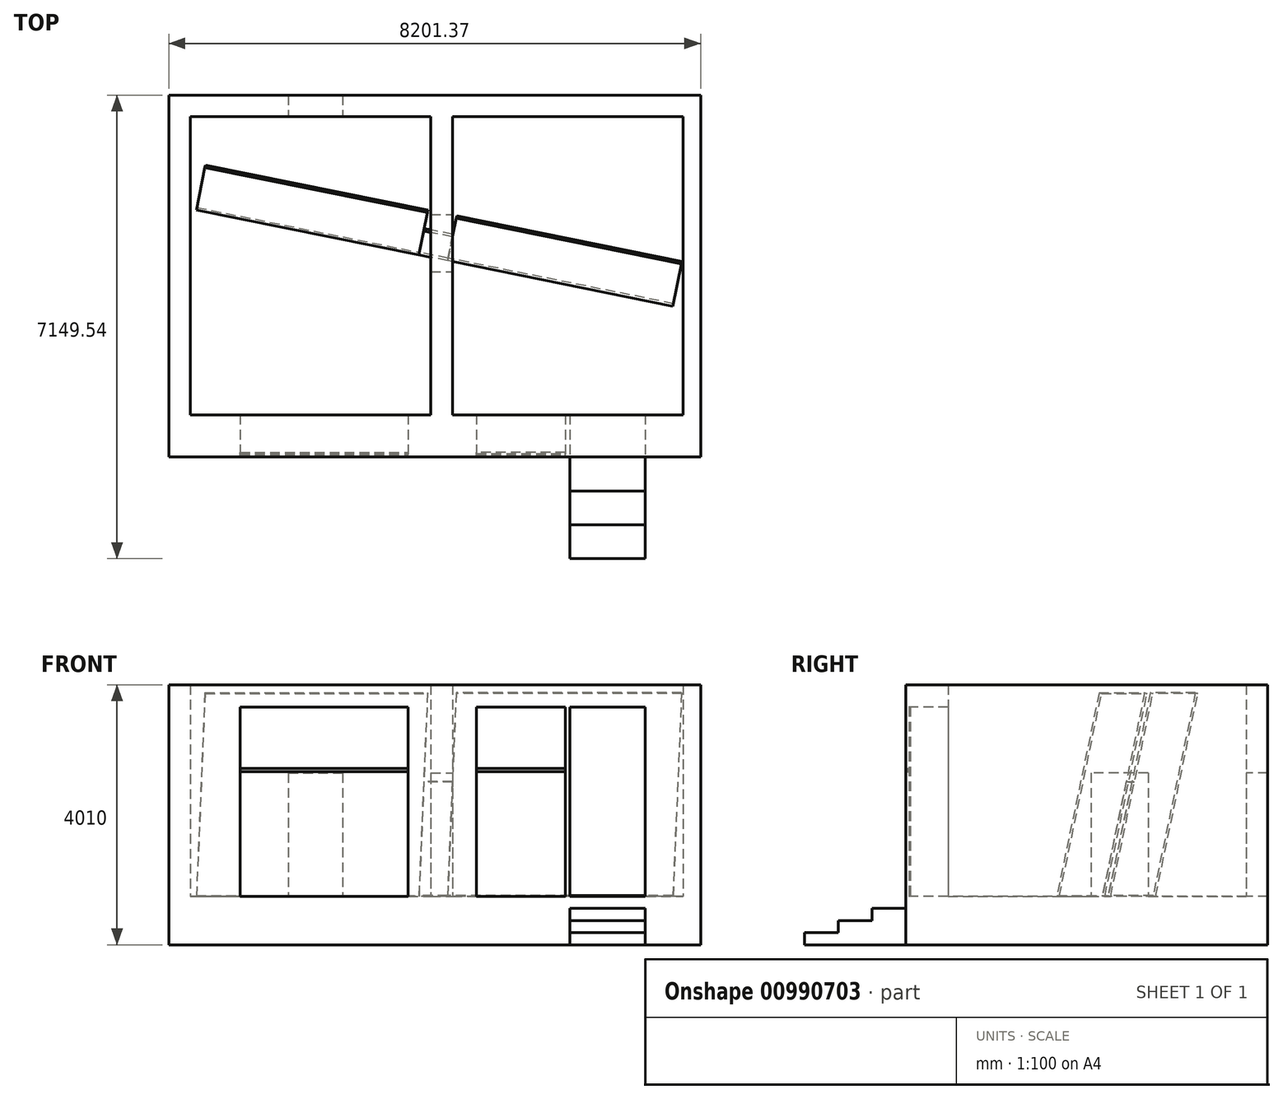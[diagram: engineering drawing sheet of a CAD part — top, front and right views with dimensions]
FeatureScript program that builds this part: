
annotation { "Feature Type Name" : "Feature", "Feature Type Description" : "" }
export const myFeature = defineFeature(function(context is Context, id is Id, definition is map)
    precondition{}
    {
        {
            var Q0;
            Q0=qCreatedBy(makeId("Top.planeOp"),FACE);
            var sketch = newSketch(context, id + "F0", { "sketchPlane" : qUnion([Q0])});
            skLineSegment(sketch, "E0", {"start": v(0, 440) * mm, "end": v(0, -440) * mm, "construction": true});
            skLineSegment(sketch, "E1", {"start": v(-165.82, 440) * mm, "end": v(165.82, 440) * mm});
            skLineSegment(sketch, "E2", {"start": v(-165.82, -440) * mm, "end": v(165.82, -440) * mm});
            skLineSegment(sketch, "E3", {"start": v(165.82, 440) * mm, "end": v(165.82, 1951.88) * mm});
            skLineSegment(sketch, "E4", {"start": v(165.82, 1951.88) * mm, "end": v(3725.82, 1951.88) * mm});
            skLineSegment(sketch, "E5", {"start": v(3725.82, 1951.88) * mm, "end": v(3725.82, -2648.12) * mm});
            skLineSegment(sketch, "E6", {"start": v(3725.82, -2648.12) * mm, "end": v(3139.18, -2648.12) * mm});
            skLineSegment(sketch, "E7", {"start": v(165.82, -2648.12) * mm, "end": v(165.82, -440) * mm});
            skLineSegment(sketch, "E8", {"start": v(-165.82, 440) * mm, "end": v(-165.82, 1951.88) * mm});
            skLineSegment(sketch, "E9", {"start": v(-165.82, 1951.88) * mm, "end": v(-1524.68, 1951.88) * mm});
            skLineSegment(sketch, "E10", {"start": v(-3875.82, 1951.88) * mm, "end": v(-3875.82, -2648.12) * mm});
            skLineSegment(sketch, "E11", {"start": v(-3875.82, -2648.12) * mm, "end": v(-3107.34, -2648.12) * mm});
            skLineSegment(sketch, "E12", {"start": v(-165.82, -2648.12) * mm, "end": v(-165.82, -440) * mm});
            skLineSegment(sketch, "E13", {"start": v(-4207.47, 2283.53) * mm, "end": v(-2364.74, 2283.53) * mm});
            skLineSegment(sketch, "E14", {"start": v(3993.9, 2283.53) * mm, "end": v(3993.9, -3299.43) * mm});
            skLineSegment(sketch, "E15", {"start": v(3993.9, -3299.43) * mm, "end": v(3139.18, -3299.43) * mm});
            skLineSegment(sketch, "E16", {"start": v(-4207.47, -3299.43) * mm, "end": v(-4207.47, 2283.53) * mm});
            skLineSegment(sketch, "E17", {"start": v(-3875.82, 1951.88) * mm, "end": v(-4207.47, 1951.88) * mm, "construction": true});
            skLineSegment(sketch, "E18", {"start": v(-3875.82, 1951.88) * mm, "end": v(-3875.82, 2283.53) * mm, "construction": true});
            skLineSegment(sketch, "E19", {"start": v(3725.82, -2648.12) * mm, "end": v(3725.82, -3299.43) * mm, "construction": true});
            skLineSegment(sketch, "E20", {"start": v(3725.82, -2648.12) * mm, "end": v(3993.9, -2648.12) * mm, "construction": true});
            skLineSegment(sketch, "E21", {"start": v(-2364.74, 2283.53) * mm, "end": v(-2364.74, 1951.88) * mm});
            skLineSegment(sketch, "E22", {"start": v(-1524.68, 2283.53) * mm, "end": v(-1524.68, 1951.88) * mm});
            skLineSegment(sketch, "E23.trimOffspring", {"start": v(-1524.68, 2283.53) * mm, "end": v(3993.9, 2283.53) * mm});
            skLineSegment(sketch, "E24.trimOffspring", {"start": v(-2364.74, 1951.88) * mm, "end": v(-3875.82, 1951.88) * mm});
            skLineSegment(sketch, "E25", {"start": v(-3107.34, -2648.12) * mm, "end": v(-3107.34, -3299.43) * mm});
            skLineSegment(sketch, "E26", {"start": v(-515.8, -2648.12) * mm, "end": v(-515.8, -3299.43) * mm});
            skLineSegment(sketch, "E27.trimOffspring", {"start": v(-515.8, -2648.12) * mm, "end": v(-165.82, -2648.12) * mm});
            skLineSegment(sketch, "E28.trimOffspring", {"start": v(-3107.34, -3299.43) * mm, "end": v(-4207.47, -3299.43) * mm});
            skLineSegment(sketch, "E29", {"start": v(537.35, -2648.12) * mm, "end": v(537.35, -3299.43) * mm});
            skLineSegment(sketch, "E30", {"start": v(1907.35, -2648.12) * mm, "end": v(1907.35, -3299.43) * mm});
            skLineSegment(sketch, "E31", {"start": v(1980.65, -2648.12) * mm, "end": v(1980.65, -3299.43) * mm});
            skLineSegment(sketch, "E32", {"start": v(3139.18, -2648.12) * mm, "end": v(3139.18, -3299.43) * mm});
            skLineSegment(sketch, "E33.trimOffspring", {"start": v(537.35, -2648.12) * mm, "end": v(165.82, -2648.12) * mm});
            skLineSegment(sketch, "E34.trimOffspring", {"start": v(537.35, -3299.43) * mm, "end": v(-515.8, -3299.43) * mm});
            skLineSegment(sketch, "E35.trimOffspring", {"start": v(1980.65, -2648.12) * mm, "end": v(1907.35, -2648.12) * mm});
            skLineSegment(sketch, "E36.trimOffspring", {"start": v(1980.65, -3299.43) * mm, "end": v(1907.35, -3299.43) * mm});
            skSolve(sketch);
        }
        {
            var Q0;
            Q0 = qSketchRegion(id + "F0", true);
            extrude(context, id + "F1", {"entities" : qUnion([Q0]), "depth" : 3260 * mm, "offsetDistance" : 25 * mm});
        }
        {
            var Q0;
            Q0=makeQuery(id+"F1.opExtrude","CAP_FACE",FACE,{"disambiguationData":[OSD([sQuery(id+"F0.wireOp",EDGE,"E10"),sQuery(id+"F0.wireOp",EDGE,"E11"),sQuery(id+"F0.wireOp",EDGE,"E13"),sQuery(id+"F0.wireOp",EDGE,"E16"),sQuery(id+"F0.wireOp",EDGE,"E21"),sQuery(id+"F0.wireOp",EDGE,"E24.trimOffspring"),sQuery(id+"F0.wireOp",EDGE,"E25"),sQuery(id+"F0.wireOp",EDGE,"E28.trimOffspring")])],"isStart":true});
            var sketch = newSketch(context, id + "F2", { "sketchPlane" : qUnion([Q0])});
            skLineSegment(sketch, "E37.bottom", {"start": v(-4207.47, 3299.43) * mm, "end": v(3993.9, 3299.43) * mm});
            skLineSegment(sketch, "E37.top", {"start": v(-4207.47, -2283.53) * mm, "end": v(3993.9, -2283.53) * mm});
            skLineSegment(sketch, "E37.left", {"start": v(-4207.47, 3299.43) * mm, "end": v(-4207.47, -2283.53) * mm});
            skLineSegment(sketch, "E37.right", {"start": v(3993.9, 3299.43) * mm, "end": v(3993.9, -2283.53) * mm});
            skSolve(sketch);
        }
        {
            var Q0;
            Q0 = qSketchRegion(id + "F2", true);
            extrude(context, id + "F3", {"entities" : qUnion([Q0]), "operationType" : NewBodyOperationType.ADD, "depth" : 750 * mm, "offsetDistance" : 25 * mm});
        }
        {
            var Q0;
            Q0=makeQuery(id+"F1.opExtrude","SWEPT_FACE",FACE,{"disambiguationData":[OSD([sQuery(id+"F0.wireOp",EDGE,"E32")])]});
            var sketch = newSketch(context, id + "F4", { "sketchPlane" : qUnion([Q0])});
            skLineSegment(sketch, "E38", {"start": v(3299.43, -187.5) * mm, "end": v(3821.63, -187.5) * mm});
            skLineSegment(sketch, "E39", {"start": v(3821.63, -187.5) * mm, "end": v(3821.63, -375) * mm});
            skLineSegment(sketch, "E40", {"start": v(3821.63, -375) * mm, "end": v(4343.82, -375) * mm});
            skLineSegment(sketch, "E41", {"start": v(4343.82, -375) * mm, "end": v(4343.82, -562.5) * mm});
            skLineSegment(sketch, "E42", {"start": v(4343.82, -562.5) * mm, "end": v(4866.01, -562.5) * mm});
            skLineSegment(sketch, "E43", {"start": v(4866.01, -562.5) * mm, "end": v(4866.01, -750) * mm});
            skLineSegment(sketch, "E44", {"start": v(4866.01, -750) * mm, "end": v(3299.43, -750) * mm});
            skLineSegment(sketch, "E45", {"start": v(3299.43, 0) * mm, "end": v(3299.43, -187.5) * mm, "construction": true});
            skLineSegment(sketch, "E46", {"start": v(3299.43, -187.5) * mm, "end": v(3299.43, -750) * mm});
            skSolve(sketch);
        }
        {
            var Q0;
            Q0 = qSketchRegion(id + "F4", true);
            var Q1;
            Q1=makeQuery(id+"F1.opExtrude","SWEPT_FACE",FACE,{"disambiguationData":[OSD([sQuery(id+"F0.wireOp",EDGE,"E31")])]});
            extrude(context, id + "F5", {"entities" : qUnion([Q0]), "operationType" : NewBodyOperationType.ADD, "endBound" : BoundingType.UP_TO_SURFACE, "depth" : 25 * mm, "endBoundEntityFace" : qUnion([Q1]), "offsetDistance" : 25 * mm});
        }
        {
            var Q0;
            Q0=makeQuery(id+"F1.opExtrude","CAP_FACE",FACE,{"disambiguationData":[OSD([sQuery(id+"F0.wireOp",EDGE,"E1"),sQuery(id+"F0.wireOp",EDGE,"E3"),sQuery(id+"F0.wireOp",EDGE,"E4"),sQuery(id+"F0.wireOp",EDGE,"E5"),sQuery(id+"F0.wireOp",EDGE,"E6"),sQuery(id+"F0.wireOp",EDGE,"E8"),sQuery(id+"F0.wireOp",EDGE,"E9"),sQuery(id+"F0.wireOp",EDGE,"E14"),sQuery(id+"F0.wireOp",EDGE,"E15"),sQuery(id+"F0.wireOp",EDGE,"E22"),sQuery(id+"F0.wireOp",EDGE,"E23.trimOffspring"),sQuery(id+"F0.wireOp",EDGE,"E32")])],"isStart":false});
            var sketch = newSketch(context, id + "F6", { "sketchPlane" : qUnion([Q0])});
            skLineSegment(sketch, "E47.bottom", {"start": v(-165.82, 440) * mm, "end": v(165.82, 440) * mm});
            skLineSegment(sketch, "E47.top", {"start": v(-165.82, -440) * mm, "end": v(165.82, -440) * mm});
            skLineSegment(sketch, "E47.left", {"start": v(-165.82, 440) * mm, "end": v(-165.82, -440) * mm});
            skLineSegment(sketch, "E47.right", {"start": v(165.82, 440) * mm, "end": v(165.82, -440) * mm});
            skSolve(sketch);
        }
        {
            var Q0;
            Q0 = qSketchRegion(id + "F6", true);
            var Q1;
            Q1=makeQuery(id+"F3.opExtrude","CAP_FACE",FACE,{"disambiguationData":[OSD([sQuery(id+"F2.wireOp",EDGE,"E37.bottom"),sQuery(id+"F2.wireOp",EDGE,"E37.top"),sQuery(id+"F2.wireOp",EDGE,"E37.left"),sQuery(id+"F2.wireOp",EDGE,"E37.right")])],"isStart":true});
            extrude(context, id + "F7", {"entities" : qUnion([Q0]), "operationType" : NewBodyOperationType.ADD, "endBound" : BoundingType.UP_TO_SURFACE, "oppositeDirection" : true, "depth" : 1120 * mm, "endBoundEntityFace" : qUnion([Q1]), "hasOffset" : true, "offsetDistance" : 1900 * mm});
        }
        {
            var Q0;
            Q0=makeQuery(id+"F1.opExtrude","CAP_FACE",FACE,{"disambiguationData":[OSD([sQuery(id+"F0.wireOp",EDGE,"E10"),sQuery(id+"F0.wireOp",EDGE,"E11"),sQuery(id+"F0.wireOp",EDGE,"E13"),sQuery(id+"F0.wireOp",EDGE,"E16"),sQuery(id+"F0.wireOp",EDGE,"E21"),sQuery(id+"F0.wireOp",EDGE,"E24.trimOffspring"),sQuery(id+"F0.wireOp",EDGE,"E25"),sQuery(id+"F0.wireOp",EDGE,"E28.trimOffspring")])],"isStart":false});
            var sketch = newSketch(context, id + "F8", { "sketchPlane" : qUnion([Q0])});
            skLineSegment(sketch, "E48.bottom", {"start": v(-3107.34, -2648.12) * mm, "end": v(-515.8, -2648.12) * mm});
            skLineSegment(sketch, "E48.top", {"start": v(-3107.34, -3299.43) * mm, "end": v(-515.8, -3299.43) * mm});
            skLineSegment(sketch, "E48.left", {"start": v(-3107.34, -2648.12) * mm, "end": v(-3107.34, -3299.43) * mm});
            skLineSegment(sketch, "E48.right", {"start": v(-515.8, -2648.12) * mm, "end": v(-515.8, -3299.43) * mm});
            skLineSegment(sketch, "E49.bottom", {"start": v(537.35, -2648.12) * mm, "end": v(1907.35, -2648.12) * mm});
            skLineSegment(sketch, "E49.top", {"start": v(537.35, -3299.43) * mm, "end": v(1907.35, -3299.43) * mm});
            skLineSegment(sketch, "E49.left", {"start": v(537.35, -2648.12) * mm, "end": v(537.35, -3299.43) * mm});
            skLineSegment(sketch, "E49.right", {"start": v(1907.35, -2648.12) * mm, "end": v(1907.35, -3299.43) * mm});
            skLineSegment(sketch, "E50.bottom", {"start": v(1980.65, -2648.12) * mm, "end": v(3139.18, -2648.12) * mm});
            skLineSegment(sketch, "E50.top", {"start": v(1980.65, -3299.43) * mm, "end": v(3139.18, -3299.43) * mm});
            skLineSegment(sketch, "E50.left", {"start": v(1980.65, -2648.12) * mm, "end": v(1980.65, -3299.43) * mm});
            skLineSegment(sketch, "E50.right", {"start": v(3139.18, -2648.12) * mm, "end": v(3139.18, -3299.43) * mm});
            skSolve(sketch);
        }
        {
            var Q0;
            Q0=makeQuery(id+"F8.imprint","IMPRINT",FACE,{"disambiguationData":[TD([[makeQuery(id+"F8.imprint","IMPRINT",EDGE,{"derivedFrom":sQuery(id+"F8.wireOp",EDGE,"E48.bottom")}),-1.0]])]});
            var Q1;
            Q1=makeQuery(id+"F8.imprint","IMPRINT",FACE,{"disambiguationData":[TD([[makeQuery(id+"F8.imprint","IMPRINT",EDGE,{"derivedFrom":sQuery(id+"F8.wireOp",EDGE,"E49.bottom")}),-1.0]])]});
            var Q2;
            Q2=makeQuery(id+"F8.imprint","IMPRINT",FACE,{"disambiguationData":[TD([[makeQuery(id+"F8.imprint","IMPRINT",EDGE,{"derivedFrom":sQuery(id+"F8.wireOp",EDGE,"E50.bottom")}),-1.0]])]});
            var Q3;
            Q3=makeQuery(id+"F3.opExtrude","CAP_FACE",FACE,{"disambiguationData":[OSD([sQuery(id+"F2.wireOp",EDGE,"E37.bottom"),sQuery(id+"F2.wireOp",EDGE,"E37.top"),sQuery(id+"F2.wireOp",EDGE,"E37.left"),sQuery(id+"F2.wireOp",EDGE,"E37.right")])],"isStart":true});
            extrude(context, id + "F9", {"entities" : qUnion([Q0, Q1, Q2]), "operationType" : NewBodyOperationType.ADD, "endBound" : BoundingType.UP_TO_SURFACE, "oppositeDirection" : true, "depth" : 25 * mm, "endBoundEntityFace" : qUnion([Q3]), "hasOffset" : true, "offsetDistance" : 2920 * mm});
        }
        {
            var Q0;
            Q0=makeQuery(id+"F9.boolean.opBoolean","MERGE",FACE,{"derivedFrom":[makeQuery(id+"F1.opExtrude","CAP_FACE",FACE,{"disambiguationData":[OSD([sQuery(id+"F0.wireOp",EDGE,"E10"),sQuery(id+"F0.wireOp",EDGE,"E11"),sQuery(id+"F0.wireOp",EDGE,"E13"),sQuery(id+"F0.wireOp",EDGE,"E16"),sQuery(id+"F0.wireOp",EDGE,"E21"),sQuery(id+"F0.wireOp",EDGE,"E24.trimOffspring"),sQuery(id+"F0.wireOp",EDGE,"E25"),sQuery(id+"F0.wireOp",EDGE,"E28.trimOffspring")])],"isStart":false}),makeQuery(id+"F1.opExtrude","CAP_FACE",FACE,{"disambiguationData":[OSD([sQuery(id+"F0.wireOp",EDGE,"E30"),sQuery(id+"F0.wireOp",EDGE,"E31"),sQuery(id+"F0.wireOp",EDGE,"E35.trimOffspring"),sQuery(id+"F0.wireOp",EDGE,"E36.trimOffspring")])],"isStart":false}),makeQuery(id+"F7.boolean.opBoolean","MERGE",FACE,{"derivedFrom":[makeQuery(id+"F1.opExtrude","CAP_FACE",FACE,{"disambiguationData":[OSD([sQuery(id+"F0.wireOp",EDGE,"E1"),sQuery(id+"F0.wireOp",EDGE,"E3"),sQuery(id+"F0.wireOp",EDGE,"E4"),sQuery(id+"F0.wireOp",EDGE,"E5"),sQuery(id+"F0.wireOp",EDGE,"E6"),sQuery(id+"F0.wireOp",EDGE,"E8"),sQuery(id+"F0.wireOp",EDGE,"E9"),sQuery(id+"F0.wireOp",EDGE,"E14"),sQuery(id+"F0.wireOp",EDGE,"E15"),sQuery(id+"F0.wireOp",EDGE,"E22"),sQuery(id+"F0.wireOp",EDGE,"E23.trimOffspring"),sQuery(id+"F0.wireOp",EDGE,"E32")])],"isStart":false}),makeQuery(id+"F1.opExtrude","CAP_FACE",FACE,{"disambiguationData":[OSD([sQuery(id+"F0.wireOp",EDGE,"E2"),sQuery(id+"F0.wireOp",EDGE,"E7"),sQuery(id+"F0.wireOp",EDGE,"E12"),sQuery(id+"F0.wireOp",EDGE,"E26"),sQuery(id+"F0.wireOp",EDGE,"E27.trimOffspring"),sQuery(id+"F0.wireOp",EDGE,"E29"),sQuery(id+"F0.wireOp",EDGE,"E33.trimOffspring"),sQuery(id+"F0.wireOp",EDGE,"E34.trimOffspring")])],"isStart":false}),makeQuery(id+"F7.opExtrude","CAP_FACE",FACE,{"disambiguationData":[OSD([sQuery(id+"F6.wireOp",EDGE,"E47.bottom"),sQuery(id+"F6.wireOp",EDGE,"E47.top"),sQuery(id+"F6.wireOp",EDGE,"E47.left"),sQuery(id+"F6.wireOp",EDGE,"E47.right")])],"isStart":true})]}),makeQuery(id+"F9.opExtrude","CAP_FACE",FACE,{"disambiguationData":[OSD([sQuery(id+"F8.wireOp",EDGE,"E48.bottom"),sQuery(id+"F8.wireOp",EDGE,"E48.top"),sQuery(id+"F8.wireOp",EDGE,"E48.left"),sQuery(id+"F8.wireOp",EDGE,"E48.right")])],"isStart":true}),makeQuery(id+"F9.opExtrude","CAP_FACE",FACE,{"disambiguationData":[OSD([sQuery(id+"F8.wireOp",EDGE,"E49.bottom"),sQuery(id+"F8.wireOp",EDGE,"E49.top"),sQuery(id+"F8.wireOp",EDGE,"E49.left"),sQuery(id+"F8.wireOp",EDGE,"E49.right")])],"isStart":true}),makeQuery(id+"F9.opExtrude","CAP_FACE",FACE,{"disambiguationData":[OSD([sQuery(id+"F8.wireOp",EDGE,"E50.bottom"),sQuery(id+"F8.wireOp",EDGE,"E50.top"),sQuery(id+"F8.wireOp",EDGE,"E50.left"),sQuery(id+"F8.wireOp",EDGE,"E50.right")])],"isStart":true})]});
            var sketch = newSketch(context, id + "F10", { "sketchPlane" : qUnion([Q0])});
            skLineSegment(sketch, "E51.bottom", {"start": v(-2364.74, 2283.53) * mm, "end": v(-1524.68, 2283.53) * mm});
            skLineSegment(sketch, "E51.top", {"start": v(-2364.74, 1951.88) * mm, "end": v(-1524.68, 1951.88) * mm});
            skLineSegment(sketch, "E51.left", {"start": v(-2364.74, 2283.53) * mm, "end": v(-2364.74, 1951.88) * mm});
            skLineSegment(sketch, "E51.right", {"start": v(-1524.68, 2283.53) * mm, "end": v(-1524.68, 1951.88) * mm});
            skSolve(sketch);
        }
        {
            var Q0;
            Q0 = qSketchRegion(id + "F10", true);
            var Q1;
            Q1=makeQuery(id+"F3.opExtrude","CAP_FACE",FACE,{"disambiguationData":[OSD([sQuery(id+"F2.wireOp",EDGE,"E37.bottom"),sQuery(id+"F2.wireOp",EDGE,"E37.top"),sQuery(id+"F2.wireOp",EDGE,"E37.left"),sQuery(id+"F2.wireOp",EDGE,"E37.right")])],"isStart":true});
            extrude(context, id + "F11", {"entities" : qUnion([Q0]), "operationType" : NewBodyOperationType.ADD, "endBound" : BoundingType.UP_TO_SURFACE, "oppositeDirection" : true, "depth" : 25 * mm, "endBoundEntityFace" : qUnion([Q1]), "hasOffset" : true, "offsetDistance" : 1900 * mm});
        }
        {
            var Q0;
            Q0=makeQuery(id+"F3.opExtrude","CAP_FACE",FACE,{"disambiguationData":[OSD([sQuery(id+"F2.wireOp",EDGE,"E37.bottom"),sQuery(id+"F2.wireOp",EDGE,"E37.top"),sQuery(id+"F2.wireOp",EDGE,"E37.left"),sQuery(id+"F2.wireOp",EDGE,"E37.right")])],"isStart":true});
            var sketch = newSketch(context, id + "F12", { "sketchPlane" : qUnion([Q0])});
            skLineSegment(sketch, "E52.bottom", {"start": v(-515.8, -3229.43) * mm, "end": v(-3107.34, -3229.43) * mm});
            skLineSegment(sketch, "E52.top", {"start": v(-515.8, -3249.43) * mm, "end": v(-3107.34, -3249.43) * mm});
            skLineSegment(sketch, "E52.left", {"start": v(-515.8, -3229.43) * mm, "end": v(-515.8, -3249.43) * mm});
            skLineSegment(sketch, "E52.right", {"start": v(-3107.34, -3229.43) * mm, "end": v(-3107.34, -3249.43) * mm});
            skLineSegment(sketch, "E53.bottom", {"start": v(537.35, -3229.43) * mm, "end": v(1907.35, -3229.43) * mm});
            skLineSegment(sketch, "E53.top", {"start": v(537.35, -3249.43) * mm, "end": v(1907.35, -3249.43) * mm});
            skLineSegment(sketch, "E53.left", {"start": v(537.35, -3229.43) * mm, "end": v(537.35, -3249.43) * mm});
            skLineSegment(sketch, "E53.right", {"start": v(1907.35, -3229.43) * mm, "end": v(1907.35, -3249.43) * mm});
            skSolve(sketch);
        }
        {
            var Q0;
            Q0 = qSketchRegion(id + "F12", true);
            var Q1;
            Q1=makeQuery(id+"F9.opExtrude","CAP_FACE",FACE,{"disambiguationData":[OSD([sQuery(id+"F8.wireOp",EDGE,"E48.bottom"),sQuery(id+"F8.wireOp",EDGE,"E48.top"),sQuery(id+"F8.wireOp",EDGE,"E48.left"),sQuery(id+"F8.wireOp",EDGE,"E48.right")])],"isStart":false});
            extrude(context, id + "F13", {"entities" : qUnion([Q0]), "endBound" : BoundingType.UP_TO_SURFACE, "depth" : 25 * mm, "endBoundEntityFace" : qUnion([Q1]), "offsetDistance" : 25 * mm});
        }
        {
            var Q0;
            Q0=makeQuery(id+"F13.opExtrude","SWEPT_FACE",FACE,{"disambiguationData":[OSD([sQuery(id+"F12.wireOp",EDGE,"E52.top")])]});
            var sketch = newSketch(context, id + "F14", { "sketchPlane" : qUnion([Q0])});
            skLineSegment(sketch, "E54.bottom", {"start": v(-3107.34, 1970) * mm, "end": v(-515.8, 1970) * mm});
            skLineSegment(sketch, "E54.top", {"start": v(-3107.34, 1920) * mm, "end": v(-515.8, 1920) * mm});
            skLineSegment(sketch, "E54.left", {"start": v(-3107.34, 1970) * mm, "end": v(-3107.34, 1920) * mm});
            skLineSegment(sketch, "E54.right", {"start": v(-515.8, 1970) * mm, "end": v(-515.8, 1920) * mm});
            skLineSegment(sketch, "E55.bottom", {"start": v(537.35, 1970) * mm, "end": v(1907.35, 1970) * mm});
            skLineSegment(sketch, "E55.top", {"start": v(537.35, 1920) * mm, "end": v(1907.35, 1920) * mm});
            skLineSegment(sketch, "E55.left", {"start": v(537.35, 1970) * mm, "end": v(537.35, 1920) * mm});
            skLineSegment(sketch, "E55.right", {"start": v(1907.35, 1970) * mm, "end": v(1907.35, 1920) * mm});
            skSolve(sketch);
        }
        {
            var Q0;
            Q0 = qSketchRegion(id + "F14", true);
            extrude(context, id + "F15", {"entities" : qUnion([Q0]), "depth" : 25 * mm, "offsetDistance" : 25 * mm});
        }
        {
            var Q0;
            Q0=makeQuery(id+"F1.opExtrude","SWEPT_FACE",FACE,{"disambiguationData":[OSD([sQuery(id+"F0.wireOp",EDGE,"E1")])]});
            var sketch = newSketch(context, id + "F16", { "sketchPlane" : qUnion([Q0])});
            skLineSegment(sketch, "E56", {"start": v(-3775.82, 0) * mm, "end": v(3625.82, 0) * mm});
            skLineSegment(sketch, "E57", {"start": v(3625.82, 0) * mm, "end": v(3625.82, 2760) * mm});
            skLineSegment(sketch, "E58", {"start": v(3625.82, 2760) * mm, "end": v(465.82, 2760) * mm});
            skLineSegment(sketch, "E59", {"start": v(465.82, 2760) * mm, "end": v(465.82, 1800) * mm});
            skLineSegment(sketch, "E60", {"start": v(465.82, 1800) * mm, "end": v(-465.82, 1800) * mm});
            skLineSegment(sketch, "E61", {"start": v(-465.82, 1800) * mm, "end": v(-465.82, 2760) * mm});
            skLineSegment(sketch, "E62", {"start": v(-465.82, 2760) * mm, "end": v(-3775.82, 2760) * mm});
            skLineSegment(sketch, "E63", {"start": v(-3775.82, 2760) * mm, "end": v(-3775.82, 0) * mm});
            skSolve(sketch);
        }
        {
            var Q0;
            Q0=qCreatedBy(makeId("Right.planeOp"),FACE);
            var sketch = newSketch(context, id + "F17", { "sketchPlane" : qUnion([Q0])});
            skLineSegment(sketch, "E64", {"start": v(-440, 16.87) * mm, "end": v(403.73, 1830.2) * mm});
            skLineSegment(sketch, "E65", {"start": v(403.73, 1830.2) * mm, "end": v(440, 1813.32) * mm});
            skLineSegment(sketch, "E66", {"start": v(440, 1813.32) * mm, "end": v(-403.73, 0) * mm});
            skLineSegment(sketch, "E67", {"start": v(-403.73, 0) * mm, "end": v(-440, 16.87) * mm});
            skSolve(sketch);
        }
        {
            var Q0;
            Q0=makeQuery(id+"F3.opExtrude","CAP_FACE",FACE,{"disambiguationData":[OSD([sQuery(id+"F2.wireOp",EDGE,"E37.bottom"),sQuery(id+"F2.wireOp",EDGE,"E37.top"),sQuery(id+"F2.wireOp",EDGE,"E37.left"),sQuery(id+"F2.wireOp",EDGE,"E37.right")])],"isStart":true});
            var sketch = newSketch(context, id + "F18", { "sketchPlane" : qUnion([Q0])});
            skLineSegment(sketch, "E68", {"start": v(-3775.82, 552.37) * mm, "end": v(3575.82, -931.99) * mm});
            skLineSegment(sketch, "E69", {"start": v(0, -440) * mm, "end": v(0, -210) * mm, "construction": true});
            skPoint(sketch, "E70", {"position": v(0, -210) * mm});
            skSolve(sketch);
        }
        {
            var Q0;
            Q0=sQuery(id+"F18.wireOp",EDGE,"E68");
            var Q1;
            Q1=sQuery(id+"F18.wireOp",VERTEX,"E70");
            cPlane(context, id + "F19", {"entities" : qUnion([Q0, Q1]), "cplaneType" : CPlaneType.LINE_POINT, "offset" : 25 * mm, "width" : 150 * mm, "height" : 150 * mm});
        }
        {
            var Q0;
            Q0=qCreatedBy(id+"F19.planeOp",FACE);
            var sketch = newSketch(context, id + "F20", { "sketchPlane" : qUnion([Q0])});
            skLineSegment(sketch, "E71", {"start": v(-205.85, 0) * mm, "end": v(168.4, 1760.67) * mm});
            skLineSegment(sketch, "E72", {"start": v(168.4, 1760.67) * mm, "end": v(129.27, 1768.98) * mm});
            skLineSegment(sketch, "E73", {"start": v(129.27, 1768.98) * mm, "end": v(-244.97, 8.32) * mm});
            skLineSegment(sketch, "E74", {"start": v(-244.97, 8.32) * mm, "end": v(-205.85, 0) * mm});
            skLineSegment(sketch, "E75", {"start": v(-205.85, 0) * mm, "end": v(311.48, 0) * mm, "construction": true});
            skSolve(sketch);
        }
        {
            var Q0;
            Q0 = qSketchRegion(id + "F20", true);
            extrude(context, id + "F21", {"entities" : qUnion([Q0]), "depth" : 100 * mm, "offsetDistance" : 25 * mm});
        }
        {
            var Q0;
            Q0 = qSketchRegion(id + "F20", true);
            extrude(context, id + "F22", {"entities" : qUnion([Q0]), "operationType" : NewBodyOperationType.ADD, "oppositeDirection" : true, "depth" : 350 * mm, "offsetDistance" : 25 * mm});
        }
        {
            var Q0;
            Q0=makeQuery(id+"F21.opExtrude","CAP_FACE",FACE,{"disambiguationData":[OSD([sQuery(id+"F20.wireOp",EDGE,"E71"),sQuery(id+"F20.wireOp",EDGE,"E72"),sQuery(id+"F20.wireOp",EDGE,"E73"),sQuery(id+"F20.wireOp",EDGE,"E74")])],"isStart":false});
            var sketch = newSketch(context, id + "F23", { "sketchPlane" : qUnion([Q0])});
            skLineSegment(sketch, "E76.0", {"start": v(129.27, 1768.98) * mm, "end": v(-244.97, 8.32) * mm});
            skLineSegment(sketch, "E76.1", {"start": v(-244.97, 8.32) * mm, "end": v(-205.85, 0) * mm});
            skLineSegment(sketch, "E76.2", {"start": v(-205.85, 0) * mm, "end": v(168.4, 1760.67) * mm});
            skLineSegment(sketch, "E77", {"start": v(129.27, 1768.98) * mm, "end": v(420.35, 3138.39) * mm});
            skLineSegment(sketch, "E78", {"start": v(420.35, 3138.39) * mm, "end": v(459.47, 3130.07) * mm});
            skLineSegment(sketch, "E79", {"start": v(459.47, 3130.07) * mm, "end": v(168.4, 1760.67) * mm});
            skSolve(sketch);
        }
        {
            var Q0;
            Q0 = qSketchRegion(id + "F23", true);
            var Q1;
            Q1=sQuery(id+"F18.wireOp",VERTEX,"E68.end");
            extrude(context, id + "F24", {"entities" : qUnion([Q0]), "endBound" : BoundingType.UP_TO_VERTEX, "depth" : 25 * mm, "endBoundEntityVertex" : qUnion([Q1]), "offsetDistance" : 25 * mm});
        }
        {
            var Q0;
            Q0=makeQuery(id+"F22.opExtrude","CAP_FACE",FACE,{"disambiguationData":[OSD([sQuery(id+"F20.wireOp",EDGE,"E71"),sQuery(id+"F20.wireOp",EDGE,"E72"),sQuery(id+"F20.wireOp",EDGE,"E73"),sQuery(id+"F20.wireOp",EDGE,"E74")])],"isStart":false});
            var sketch = newSketch(context, id + "F25", { "sketchPlane" : qUnion([Q0])});
            skLineSegment(sketch, "E80.0", {"start": v(-129.27, 1768.98) * mm, "end": v(244.97, 8.32) * mm});
            skLineSegment(sketch, "E80.1", {"start": v(244.97, 8.32) * mm, "end": v(205.85, 0) * mm});
            skLineSegment(sketch, "E80.2", {"start": v(205.85, 0) * mm, "end": v(-168.4, 1760.67) * mm});
            skLineSegment(sketch, "E80.3", {"start": v(-129.27, 1768.98) * mm, "end": v(-420.35, 3138.39) * mm});
            skLineSegment(sketch, "E80.4", {"start": v(-420.35, 3138.39) * mm, "end": v(-459.47, 3130.07) * mm});
            skLineSegment(sketch, "E80.5", {"start": v(-459.47, 3130.07) * mm, "end": v(-168.4, 1760.67) * mm});
            skSolve(sketch);
        }
        {
            var Q0;
            Q0 = qSketchRegion(id + "F25", true);
            var Q1;
            Q1=sQuery(id+"F18.wireOp",VERTEX,"E68.start");
            extrude(context, id + "F26", {"entities" : qUnion([Q0]), "endBound" : BoundingType.UP_TO_VERTEX, "depth" : 25 * mm, "endBoundEntityVertex" : qUnion([Q1]), "offsetDistance" : 25 * mm});
        }
    });
